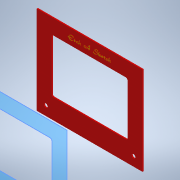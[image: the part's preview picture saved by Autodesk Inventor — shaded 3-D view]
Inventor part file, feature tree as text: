
AUTODESK INVENTOR PART (.ipt)
format: ipt  version: 2022 (Build 260153000, 153)  size: 523,776 bytes
history: native  units: mm
features: sketch x4, extrude x3, other x3, hole x1, mirror x1, reference x1
ambient origin geometry x8: Origin, YZ Plane, XZ Plane, XY Plane, X Axis, Y Axis, Z Axis, Center Point
bodies: Solid1 (feature_tree)
feature tree (13):
  extrude  "Extrusion1"  Depth=441.771875mm
  extrude  "Extrusion2"  Depth=267.66875mm
  hole  "Hole1"  [1 undecoded]
  mirror  "Mirror1"
  extrude  "Extrusion4"  TaperAngle=0.0deg  [1 undecoded]
  sketch  "Sketch1"  dims[d0=528.23125mm d1=441.771875mm]
  sketch  "Sketch2"  dims[d2=6.0mm d3=0.0mm d4=267.66875mm]
  sketch  "Sketch3"  dims[d5=379.0mm d6=74.615625mm]
  sketch  "Sketch4"  dims[d7=8.290625mm d8=0.0mm d9=0.0mm d10=45.00625mm d11=45.00625mm d12=19.0mm d13=6.0mm d14=4.0mm d15=2.0mm d16=90.0deg d17=8.0mm d18=20.594885mm d21=2.0mm d22=0.0mm]
  reference  "Reference1"
  other  "<userpath>\Documents\Inventor\etchasketch\etchasketch.iam"
  other  "etchasketch.iam"
  other  "skærm:1"
note: 2 required parameter values undecoded (feature->parameter linkage not recoverable at this tier; creation-order binding heuristic only, values carry confidence <= 0.55)
